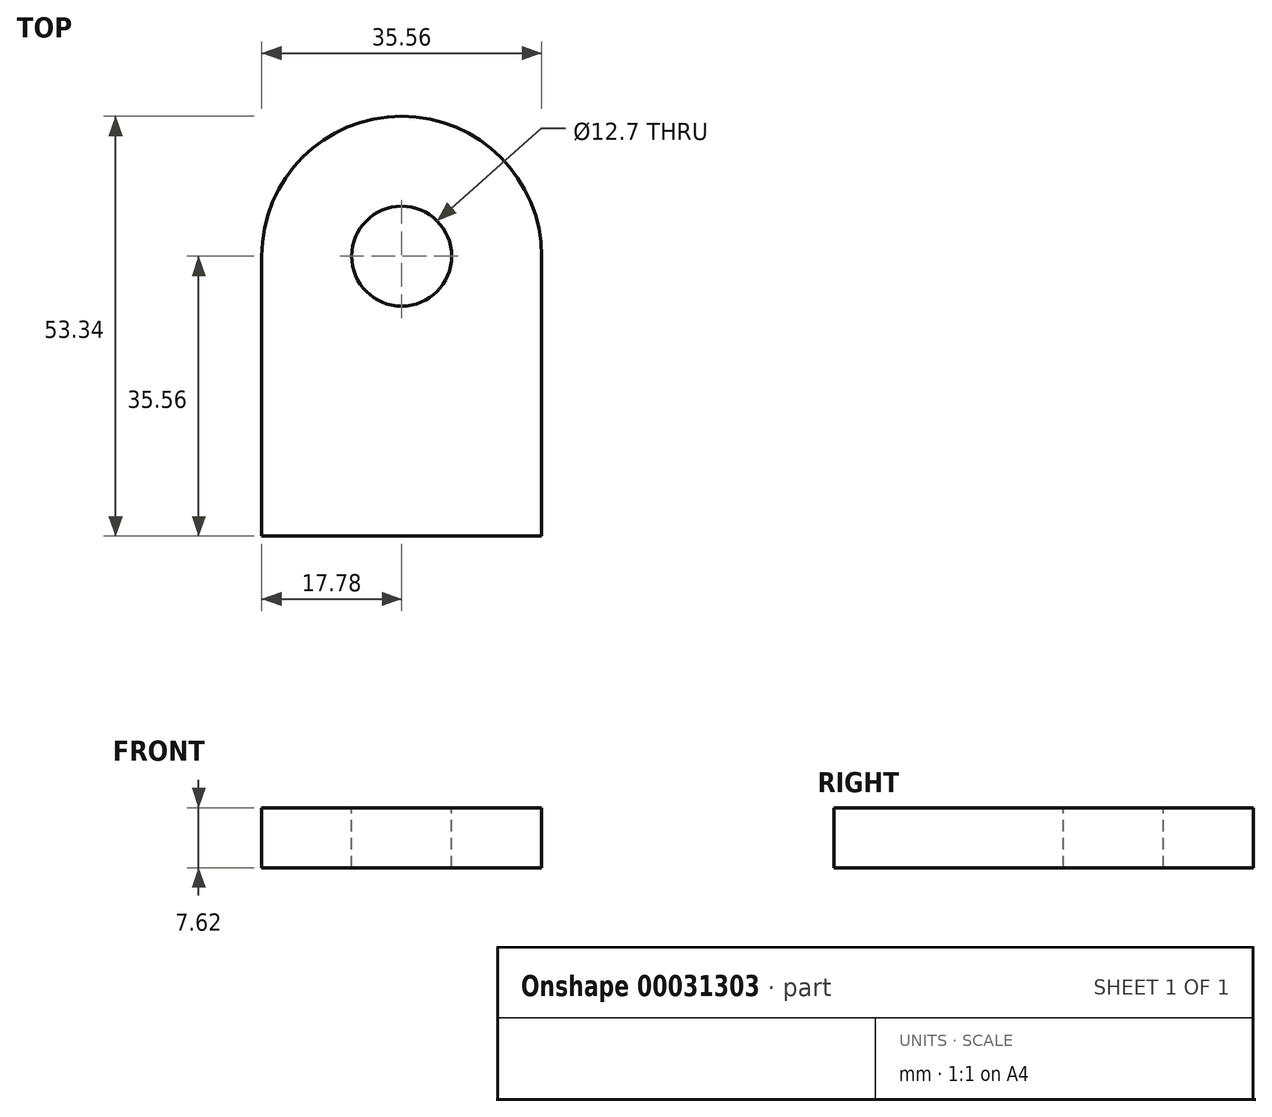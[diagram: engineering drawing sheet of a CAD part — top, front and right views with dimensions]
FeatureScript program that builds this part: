
annotation { "Feature Type Name" : "Feature", "Feature Type Description" : "" }
export const myFeature = defineFeature(function(context is Context, id is Id, definition is map)
    precondition{}
    {
        {
            var Q0;
            Q0=qCreatedBy(makeId("Top.planeOp"),FACE);
            var sketch = newSketch(context, id + "F0", { "sketchPlane" : qUnion([Q0])});
            skLineSegment(sketch, "E0.top", {"start": v(0, -35.56) * mm, "end": v(35.56, -35.56) * mm});
            skLineSegment(sketch, "E0.left", {"start": v(0, 0) * mm, "end": v(0, -35.56) * mm});
            skLineSegment(sketch, "E0.right", {"start": v(35.56, 0) * mm, "end": v(35.56, -35.56) * mm});
            skArc(sketch, "E1", {"start": v(35.56, 0) * mm, "mid": v(17.78, 17.78) * mm, "end": v(0, 0) * mm});
            skSolve(sketch);
        }
        {
            var Q0;
            Q0=makeQuery(id+"F0.imprint","IMPRINT",FACE,{"disambiguationData":[TD([[makeQuery(id+"F0.imprint","IMPRINT",EDGE,{"derivedFrom":sQuery(id+"F0.wireOp",EDGE,"E0.top")}),1.0]])]});
            extrude(context, id + "F1", {"entities" : qUnion([Q0]), "depth" : 7.62 * mm});
        }
        {
            var Q0;
            Q0=makeQuery(id+"F1.opExtrude","CAP_FACE",FACE,{"disambiguationData":[OSD([sQuery(id+"F0.wireOp",EDGE,"E0.top"),sQuery(id+"F0.wireOp",EDGE,"E0.left"),sQuery(id+"F0.wireOp",EDGE,"E0.right"),sQuery(id+"F0.wireOp",EDGE,"E1")])],"isStart":false});
            var sketch = newSketch(context, id + "F2", { "sketchPlane" : qUnion([Q0])});
            skCircle(sketch, "E2", {"center": v(17.78, 0) * mm, "radius": 6.35 * mm});
            skSolve(sketch);
        }
        {
            var Q0;
            Q0=makeQuery(id+"F2.imprint","IMPRINT",FACE,{"disambiguationData":[TD([[makeQuery(id+"F2.imprint","IMPRINT",EDGE,{"derivedFrom":sQuery(id+"F2.wireOp",EDGE,"E2")}),1.0]])]});
            extrude(context, id + "F3", {"entities" : qUnion([Q0]), "operationType" : NewBodyOperationType.REMOVE, "oppositeDirection" : true, "depth" : 25.4 * mm});
        }
    });
